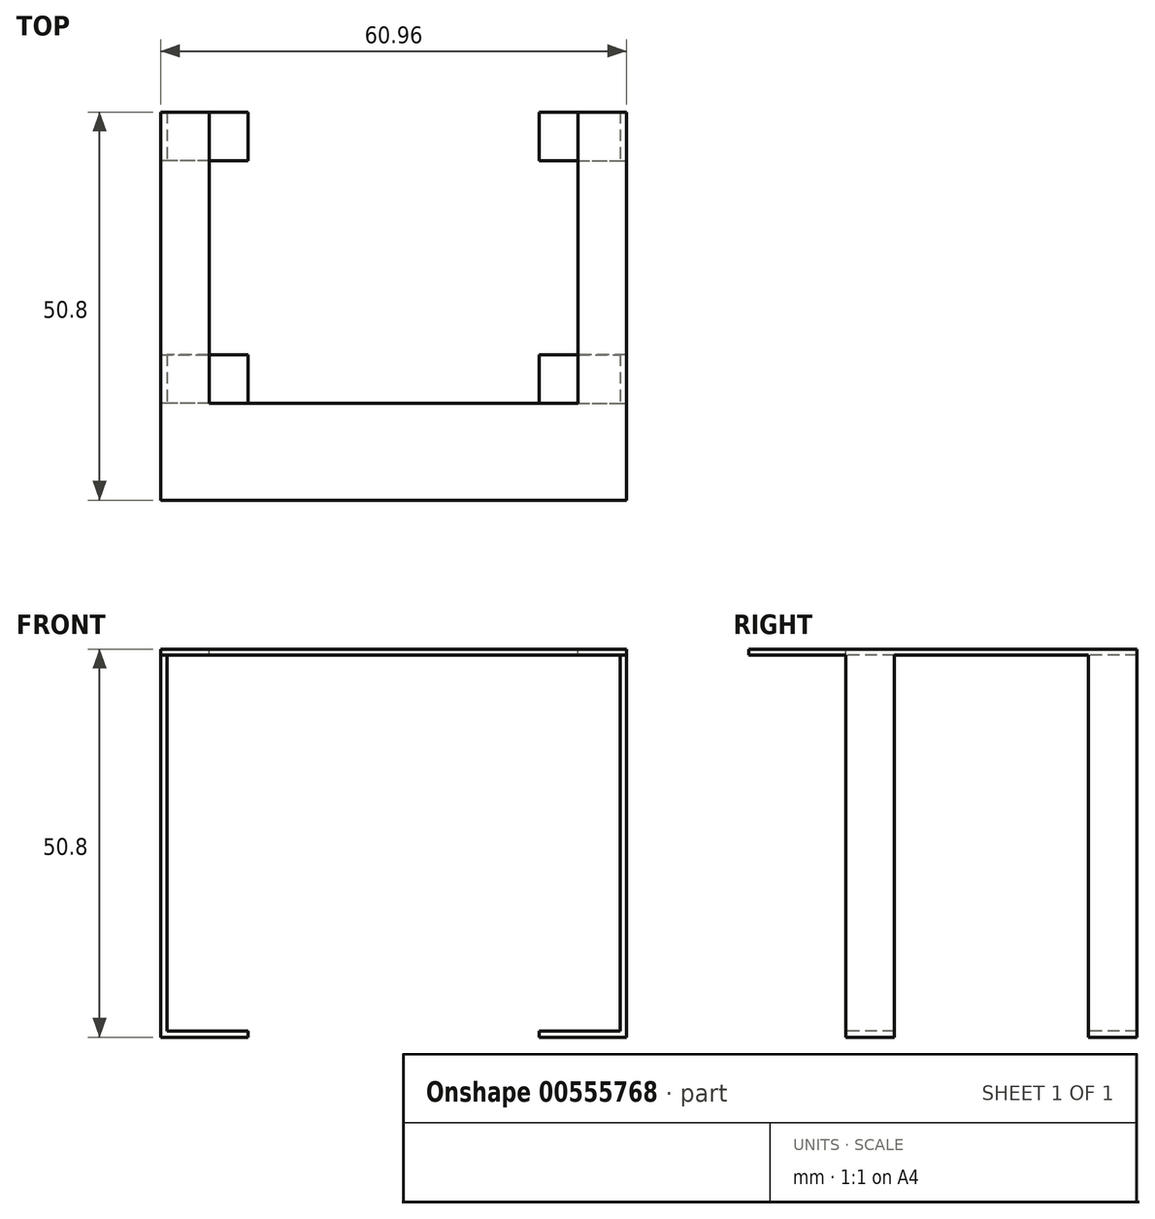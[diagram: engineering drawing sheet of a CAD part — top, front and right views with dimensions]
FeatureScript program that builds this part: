
annotation { "Feature Type Name" : "Feature", "Feature Type Description" : "" }
export const myFeature = defineFeature(function(context is Context, id is Id, definition is map)
    precondition{}
    {
        {
            var Q0;
            Q0=qCreatedBy(makeId("Top.planeOp"),FACE);
            var sketch = newSketch(context, id + "F0", { "sketchPlane" : qUnion([Q0])});
            skLineSegment(sketch, "E0.bottom", {"start": v(0, 0) * mm, "end": v(60.96, 0) * mm});
            skLineSegment(sketch, "E0.top", {"start": v(0, 50.8) * mm, "end": v(60.96, 50.8) * mm});
            skLineSegment(sketch, "E0.left", {"start": v(0, 0) * mm, "end": v(0, 50.8) * mm});
            skLineSegment(sketch, "E0.right", {"start": v(60.96, 0) * mm, "end": v(60.96, 50.8) * mm});
            skSolve(sketch);
        }
        {
            var Q0;
            Q0 = qSketchRegion(id + "F0", true);
            extrude(context, id + "F1", {"entities" : qUnion([Q0]), "depth" : 0.81 * mm, "offsetDistance" : 25.4 * mm});
        }
        {
            var Q0;
            Q0=makeQuery(id+"F1.opExtrude","CAP_FACE",FACE,{"disambiguationData":[OSD([sQuery(id+"F0.wireOp",EDGE,"E0.bottom"),sQuery(id+"F0.wireOp",EDGE,"E0.top"),sQuery(id+"F0.wireOp",EDGE,"E0.left"),sQuery(id+"F0.wireOp",EDGE,"E0.right")])],"isStart":false});
            var sketch = newSketch(context, id + "F2", { "sketchPlane" : qUnion([Q0])});
            skLineSegment(sketch, "E1", {"start": v(0, 50.8) * mm, "end": v(6.35, 50.8) * mm});
            skLineSegment(sketch, "E2", {"start": v(6.35, 50.8) * mm, "end": v(6.35, 12.7) * mm});
            skLineSegment(sketch, "E3", {"start": v(6.35, 12.7) * mm, "end": v(54.6, 12.7) * mm});
            skLineSegment(sketch, "E4", {"start": v(54.6, 12.7) * mm, "end": v(54.6, 50.8) * mm});
            skLineSegment(sketch, "E5", {"start": v(54.6, 50.8) * mm, "end": v(6.35, 50.8) * mm});
            skSolve(sketch);
        }
        {
            var Q0;
            Q0 = qSketchRegion(id + "F2", true);
            extrude(context, id + "F3", {"entities" : qUnion([Q0]), "operationType" : NewBodyOperationType.REMOVE, "oppositeDirection" : true, "depth" : 25.4 * mm, "offsetDistance" : 25.4 * mm});
        }
        {
            var Q0;
            Q0=makeQuery(id+"F1.opExtrude","CAP_FACE",FACE,{"disambiguationData":[OSD([sQuery(id+"F0.wireOp",EDGE,"E0.bottom"),sQuery(id+"F0.wireOp",EDGE,"E0.top"),sQuery(id+"F0.wireOp",EDGE,"E0.left"),sQuery(id+"F0.wireOp",EDGE,"E0.right")])],"isStart":false});
            var sketch = newSketch(context, id + "F4", { "sketchPlane" : qUnion([Q0])});
            skLineSegment(sketch, "E6", {"start": v(0, 50.8) * mm, "end": v(0.81, 50.8) * mm});
            skLineSegment(sketch, "E7", {"start": v(0.81, 50.8) * mm, "end": v(0.81, 44.45) * mm});
            skLineSegment(sketch, "E8", {"start": v(0.81, 44.45) * mm, "end": v(0, 44.45) * mm});
            skLineSegment(sketch, "E9", {"start": v(0, 44.45) * mm, "end": v(0, 50.8) * mm});
            skLineSegment(sketch, "E10", {"start": v(60.96, 50.8) * mm, "end": v(60.15, 50.8) * mm});
            skLineSegment(sketch, "E11", {"start": v(60.15, 50.8) * mm, "end": v(60.15, 44.45) * mm});
            skLineSegment(sketch, "E12", {"start": v(60.15, 44.45) * mm, "end": v(60.96, 44.45) * mm});
            skLineSegment(sketch, "E13", {"start": v(60.96, 44.45) * mm, "end": v(60.96, 50.8) * mm});
            skLineSegment(sketch, "E14", {"start": v(0, 19.05) * mm, "end": v(0.81, 19.05) * mm});
            skLineSegment(sketch, "E15", {"start": v(0.81, 19.05) * mm, "end": v(0.81, 12.7) * mm});
            skLineSegment(sketch, "E16", {"start": v(0.81, 12.7) * mm, "end": v(0, 12.7) * mm});
            skLineSegment(sketch, "E17", {"start": v(0, 12.7) * mm, "end": v(0, 19.05) * mm});
            skLineSegment(sketch, "E18", {"start": v(60.96, 19.05) * mm, "end": v(60.15, 19.05) * mm});
            skLineSegment(sketch, "E19", {"start": v(60.15, 19.05) * mm, "end": v(60.15, 12.7) * mm});
            skLineSegment(sketch, "E20", {"start": v(60.15, 12.7) * mm, "end": v(60.96, 12.7) * mm});
            skLineSegment(sketch, "E21", {"start": v(60.96, 12.7) * mm, "end": v(60.96, 19.05) * mm});
            skSolve(sketch);
        }
        {
            var Q0;
            Q0 = qSketchRegion(id + "F4", true);
            extrude(context, id + "F5", {"entities" : qUnion([Q0]), "operationType" : NewBodyOperationType.ADD, "oppositeDirection" : true, "depth" : 50.8 * mm, "offsetDistance" : 25.4 * mm});
        }
        {
            var Q0;
            Q0=makeQuery(id+"F5.boolean.opBoolean","MERGE",FACE,{"derivedFrom":[makeQuery(id+"F1.opExtrude","SWEPT_FACE",FACE,{"disambiguationData":[OSD([sQuery(id+"F0.wireOp",EDGE,"E0.right")])]}),makeQuery(id+"F5.opExtrude","SWEPT_FACE",FACE,{"disambiguationData":[OSD([sQuery(id+"F4.wireOp",EDGE,"E13")])]}),makeQuery(id+"F5.opExtrude","SWEPT_FACE",FACE,{"disambiguationData":[OSD([sQuery(id+"F4.wireOp",EDGE,"E21")])]})]});
            var sketch = newSketch(context, id + "F6", { "sketchPlane" : qUnion([Q0])});
            skLineSegment(sketch, "E22", {"start": v(12.7, -49.99) * mm, "end": v(12.7, -49.17) * mm});
            skLineSegment(sketch, "E23", {"start": v(12.7, -49.17) * mm, "end": v(19.05, -49.17) * mm});
            skLineSegment(sketch, "E24", {"start": v(19.05, -49.17) * mm, "end": v(19.05, -49.99) * mm});
            skLineSegment(sketch, "E25", {"start": v(19.05, -49.99) * mm, "end": v(12.7, -49.99) * mm});
            skLineSegment(sketch, "E26", {"start": v(44.45, -49.99) * mm, "end": v(44.45, -49.17) * mm});
            skLineSegment(sketch, "E27", {"start": v(44.45, -49.17) * mm, "end": v(50.8, -49.17) * mm});
            skLineSegment(sketch, "E28", {"start": v(50.8, -49.17) * mm, "end": v(50.8, -49.99) * mm});
            skLineSegment(sketch, "E29", {"start": v(50.8, -49.99) * mm, "end": v(44.45, -49.99) * mm});
            skSolve(sketch);
        }
        {
            var Q0;
            Q0 = qSketchRegion(id + "F6", true);
            extrude(context, id + "F7", {"entities" : qUnion([Q0]), "operationType" : NewBodyOperationType.ADD, "oppositeDirection" : true, "depth" : 11.43 * mm, "offsetDistance" : 25.4 * mm});
        }
        {
            var Q0;
            Q0=makeQuery(id+"F5.boolean.opBoolean","MERGE",FACE,{"derivedFrom":[makeQuery(id+"F1.opExtrude","SWEPT_FACE",FACE,{"disambiguationData":[OSD([sQuery(id+"F0.wireOp",EDGE,"E0.left")])]}),makeQuery(id+"F5.opExtrude","SWEPT_FACE",FACE,{"disambiguationData":[OSD([sQuery(id+"F4.wireOp",EDGE,"E9")])]}),makeQuery(id+"F5.opExtrude","SWEPT_FACE",FACE,{"disambiguationData":[OSD([sQuery(id+"F4.wireOp",EDGE,"E17")])]})]});
            var sketch = newSketch(context, id + "F8", { "sketchPlane" : qUnion([Q0])});
            skLineSegment(sketch, "E30", {"start": v(-50.8, -49.99) * mm, "end": v(-50.8, -49.17) * mm});
            skLineSegment(sketch, "E31", {"start": v(-50.8, -49.17) * mm, "end": v(-44.45, -49.17) * mm});
            skLineSegment(sketch, "E32", {"start": v(-44.45, -49.17) * mm, "end": v(-44.45, -49.99) * mm});
            skLineSegment(sketch, "E33", {"start": v(-44.45, -49.99) * mm, "end": v(-50.8, -49.99) * mm});
            skLineSegment(sketch, "E34", {"start": v(-19.05, -49.99) * mm, "end": v(-19.05, -49.17) * mm});
            skLineSegment(sketch, "E35", {"start": v(-19.05, -49.17) * mm, "end": v(-12.7, -49.17) * mm});
            skLineSegment(sketch, "E36", {"start": v(-12.7, -49.17) * mm, "end": v(-12.7, -49.99) * mm});
            skLineSegment(sketch, "E37", {"start": v(-12.7, -49.99) * mm, "end": v(-19.05, -49.99) * mm});
            skSolve(sketch);
        }
        {
            var Q0;
            Q0 = qSketchRegion(id + "F8", true);
            extrude(context, id + "F9", {"entities" : qUnion([Q0]), "operationType" : NewBodyOperationType.ADD, "oppositeDirection" : true, "depth" : 11.43 * mm, "offsetDistance" : 25.4 * mm});
        }
    });
